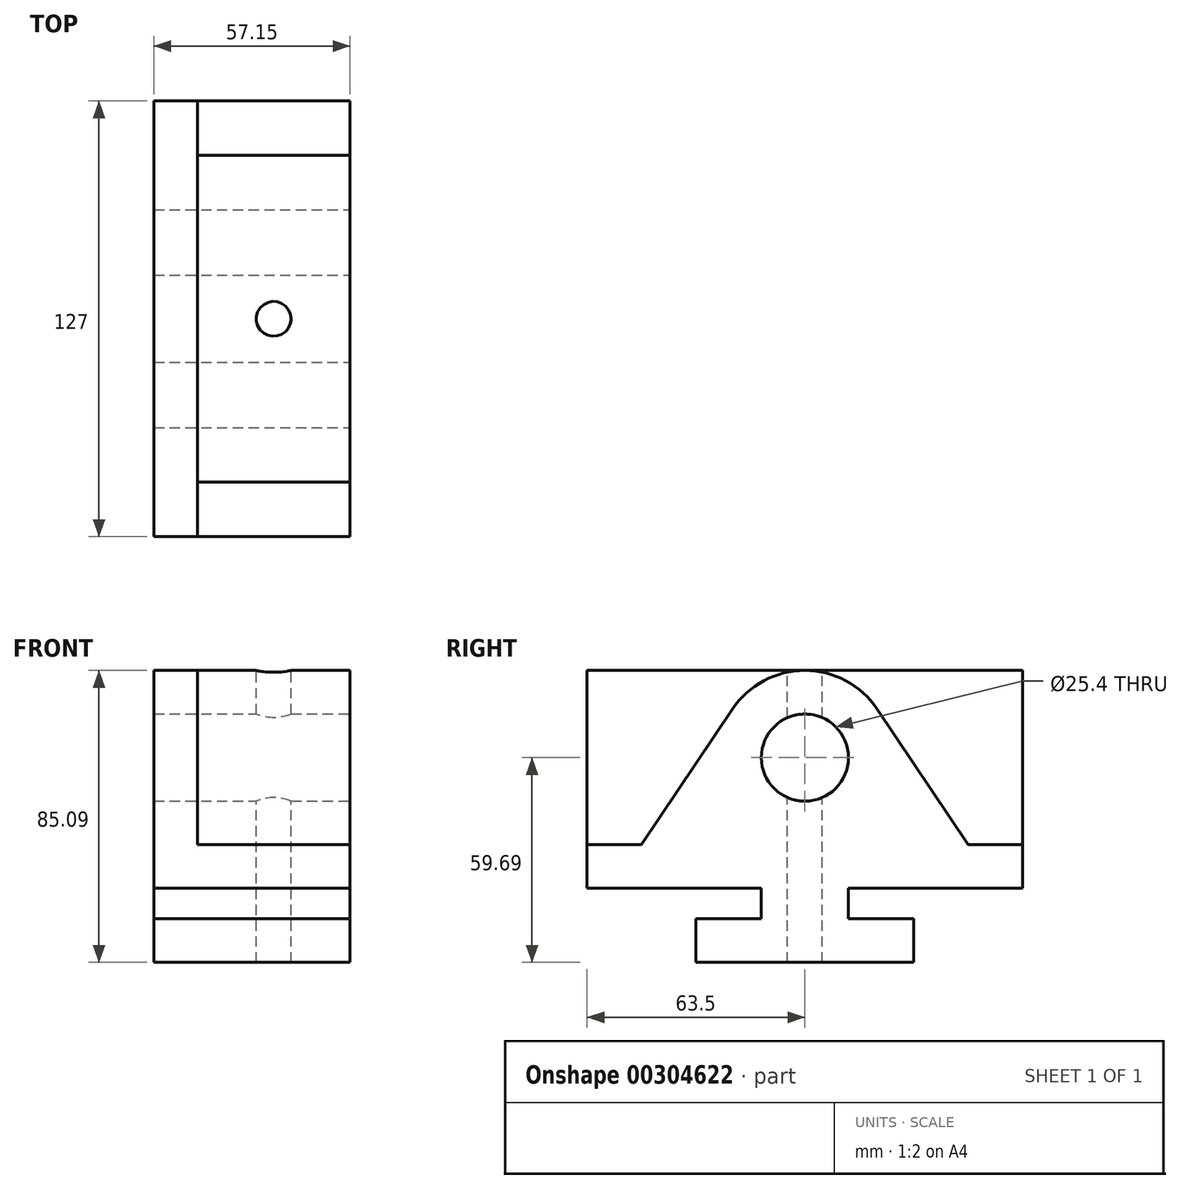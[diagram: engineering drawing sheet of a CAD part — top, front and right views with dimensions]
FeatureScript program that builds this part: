
annotation { "Feature Type Name" : "Feature", "Feature Type Description" : "" }
export const myFeature = defineFeature(function(context is Context, id is Id, definition is map)
    precondition{}
    {
        {
            var Q0;
            Q0=qCreatedBy(makeId("Right.planeOp"),FACE);
            var sketch = newSketch(context, id + "F0", { "sketchPlane" : qUnion([Q0])});
            skLineSegment(sketch, "E0.bottom", {"start": v(0, 0) * mm, "end": v(127, 0) * mm});
            skLineSegment(sketch, "E0.top", {"start": v(0, 85.1) * mm, "end": v(127, 85.1) * mm});
            skLineSegment(sketch, "E0.left", {"start": v(0, 0) * mm, "end": v(0, 85.1) * mm});
            skLineSegment(sketch, "E0.right", {"start": v(127, 0) * mm, "end": v(127, 85.1) * mm});
            skLineSegment(sketch, "E1", {"start": v(63.5, 0) * mm, "end": v(63.5, 85.1) * mm, "construction": true});
            skLineSegment(sketch, "E2", {"start": v(0, 0) * mm, "end": v(0, 34.3) * mm, "construction": true});
            skLineSegment(sketch, "E3", {"start": v(0, 34.3) * mm, "end": v(15.87, 34.3) * mm});
            skLineSegment(sketch, "E4", {"start": v(127, 34.3) * mm, "end": v(111.12, 34.3) * mm});
            skLineSegment(sketch, "E5", {"start": v(0, 34.3) * mm, "end": v(0, 85.1) * mm, "construction": true});
            skCircle(sketch, "E6", {"center": v(63.5, 59.7) * mm, "radius": 12.7 * mm});
            skPoint(sketch, "E6.centerSnap0", {"position": v(0, 59.7) * mm});
            skArc(sketch, "E7", {"start": v(84.6, 73.84) * mm, "mid": v(63.5, 85.1) * mm, "end": v(42.4, 73.84) * mm});
            skLineSegment(sketch, "E8", {"start": v(15.87, 34.3) * mm, "end": v(42.4, 73.84) * mm});
            skLineSegment(sketch, "E9", {"start": v(84.6, 73.84) * mm, "end": v(111.12, 34.3) * mm});
            skLineSegment(sketch, "E10.left", {"start": v(0, 85.1) * mm, "end": v(0, 0) * mm});
            skLineSegment(sketch, "E10.right", {"start": v(127, 85.1) * mm, "end": v(127, 0) * mm});
            skLineSegment(sketch, "E11", {"start": v(63.5, 0) * mm, "end": v(95.25, 0) * mm});
            skLineSegment(sketch, "E12", {"start": v(95.25, 0) * mm, "end": v(95.25, 12.7) * mm});
            skLineSegment(sketch, "E13", {"start": v(95.25, 12.7) * mm, "end": v(76.2, 12.7) * mm});
            skLineSegment(sketch, "E14", {"start": v(76.2, 12.7) * mm, "end": v(76.2, 21.59) * mm});
            skLineSegment(sketch, "E15", {"start": v(76.2, 21.59) * mm, "end": v(127, 21.59) * mm});
            skLineSegment(sketch, "E16.MirrorCS", {"start": v(31.75, 0) * mm, "end": v(31.75, 12.7) * mm});
            skLineSegment(sketch, "E17.MirrorCS", {"start": v(31.75, 12.7) * mm, "end": v(50.8, 12.7) * mm});
            skLineSegment(sketch, "E18.MirrorCS", {"start": v(50.8, 21.59) * mm, "end": v(0, 21.59) * mm});
            skLineSegment(sketch, "E19", {"start": v(31.75, 0) * mm, "end": v(63.5, 0) * mm});
            skLineSegment(sketch, "E20", {"start": v(50.8, 21.59) * mm, "end": v(50.8, 12.7) * mm});
            skSolve(sketch);
        }
        {
            var Q0;
            {var subQ6=sQuery(id+"F0.wireOp",EDGE,"E4");Q0=makeQuery(id+"F0.imprint","IMPRINT",FACE,{"disambiguationData":[TD([[makeQuery(id+"F0.imprint","IMPRINT",EDGE,{"derivedFrom":subQ6}),-1.0]])]});}
            var Q1;
            {var subQ6=sQuery(id+"F0.wireOp",EDGE,"E3");Q1=makeQuery(id+"F0.imprint","IMPRINT",FACE,{"disambiguationData":[TD([[makeQuery(id+"F0.imprint","IMPRINT",EDGE,{"derivedFrom":subQ6}),-1.0]])]});}
            var Q2;
            {var subQ6=sQuery(id+"F0.wireOp",EDGE,"E3");Q2=makeQuery(id+"F0.imprint","IMPRINT",FACE,{"disambiguationData":[TD([[makeQuery(id+"F0.imprint","IMPRINT",EDGE,{"derivedFrom":subQ6}),1.0]])]});}
            extrude(context, id + "F1", {"entities" : qUnion([Q0, Q1, Q2]), "oppositeDirection" : true, "depth" : 57.15 * mm});
        }
        {
            var Q0;
            {var subQ6=sQuery(id+"F0.wireOp",EDGE,"E3");Q0=makeQuery(id+"F0.imprint","IMPRINT",FACE,{"disambiguationData":[TD([[makeQuery(id+"F0.imprint","IMPRINT",EDGE,{"derivedFrom":subQ6}),1.0]])]});}
            var Q1;
            {var subQ6=sQuery(id+"F0.wireOp",EDGE,"E4");Q1=makeQuery(id+"F0.imprint","IMPRINT",FACE,{"disambiguationData":[TD([[makeQuery(id+"F0.imprint","IMPRINT",EDGE,{"derivedFrom":subQ6}),-1.0]])]});}
            extrude(context, id + "F2", {"entities" : qUnion([Q0, Q1]), "operationType" : NewBodyOperationType.REMOVE, "oppositeDirection" : true, "depth" : 44.45 * mm});
        }
        {
            var Q0;
            {var subQ0=sQuery(id+"F0.wireOp",EDGE,"E16.MirrorCS");Q0=makeQuery(id+"F0.imprint","IMPRINT",FACE,{"disambiguationData":[TD([[makeQuery(id+"F0.imprint","IMPRINT",EDGE,{"derivedFrom":subQ0}),1.0]])]});}
            var Q1;
            {var subQ0=sQuery(id+"F0.wireOp",EDGE,"E12");Q1=makeQuery(id+"F0.imprint","IMPRINT",FACE,{"disambiguationData":[TD([[makeQuery(id+"F0.imprint","IMPRINT",EDGE,{"derivedFrom":subQ0}),-1.0]])]});}
            extrude(context, id + "F3", {"entities" : qUnion([Q0, Q1]), "operationType" : NewBodyOperationType.REMOVE, "oppositeDirection" : true, "depth" : 57.15 * mm});
        }
        {
            var Q0;
            Q0=makeQuery(id+"F1.opExtrude","SWEPT_FACE",FACE,{"disambiguationData":[OSD([sQuery(id+"F0.wireOp",EDGE,"E0.top")])]});
            var sketch = newSketch(context, id + "F4", { "sketchPlane" : qUnion([Q0])});
            skCircle(sketch, "E21", {"center": v(-22.23, 63.5) * mm, "radius": 5.08 * mm});
            skSolve(sketch);
        }
        {
            var Q0;
            Q0=makeQuery(id+"F4.imprint","IMPRINT",FACE,{"disambiguationData":[TD([[makeQuery(id+"F4.imprint","IMPRINT",EDGE,{"derivedFrom":sQuery(id+"F4.wireOp",EDGE,"E21")}),1.0]])]});
            extrude(context, id + "F5", {"entities" : qUnion([Q0]), "operationType" : NewBodyOperationType.REMOVE, "oppositeDirection" : true, "depth" : 85.1 * mm});
        }
    });
